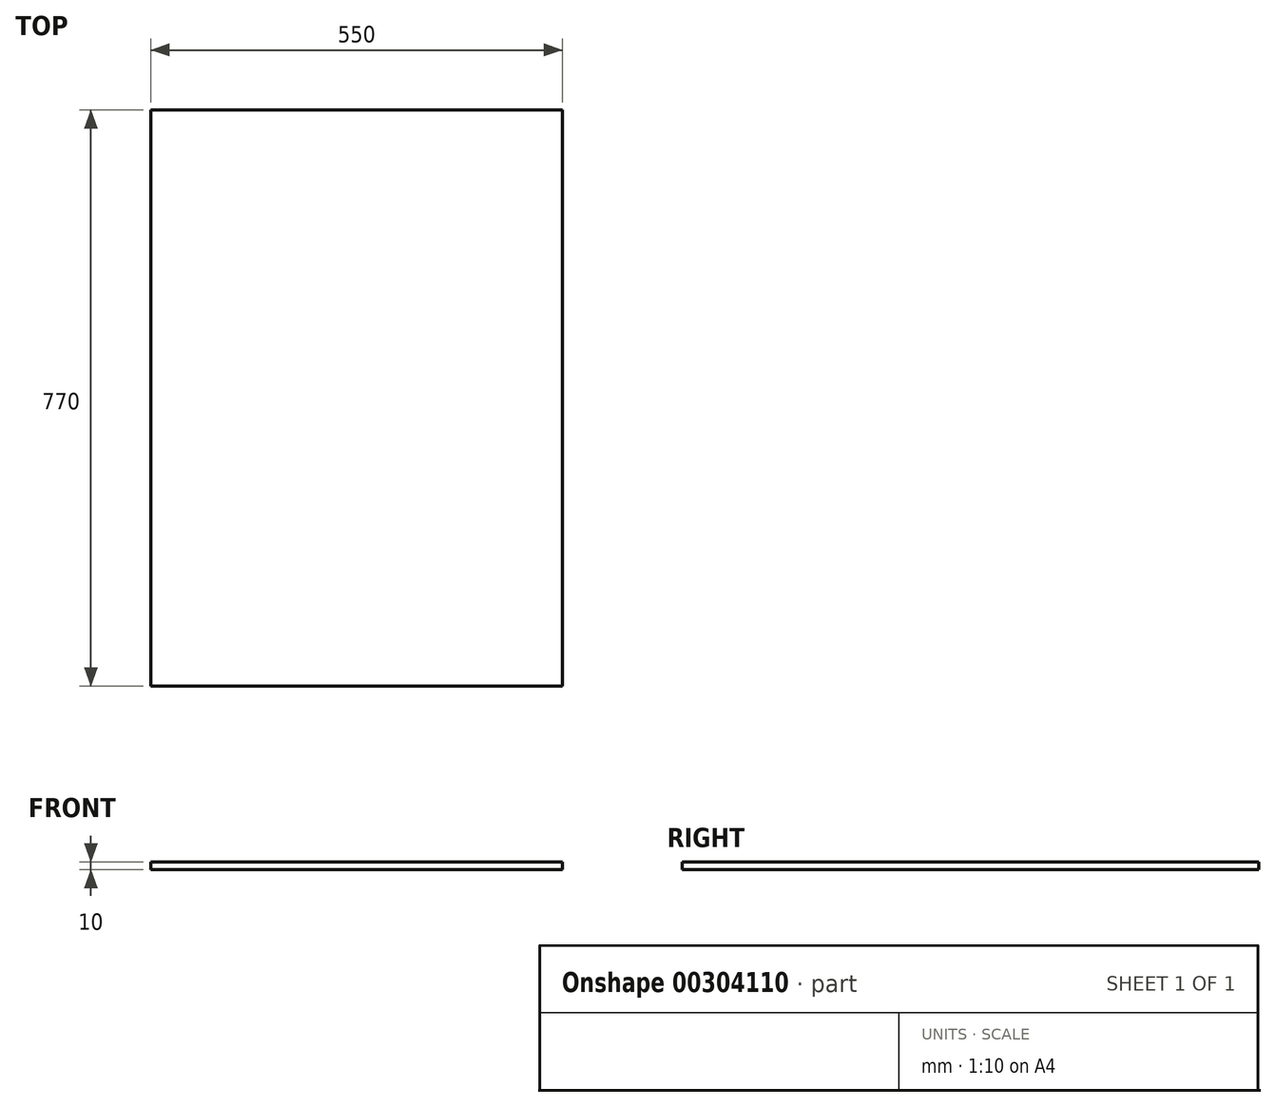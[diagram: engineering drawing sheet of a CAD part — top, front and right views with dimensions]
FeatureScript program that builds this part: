
annotation { "Feature Type Name" : "Feature", "Feature Type Description" : "" }
export const myFeature = defineFeature(function(context is Context, id is Id, definition is map)
    precondition{}
    {
        {
            var Q0;
            Q0=qCreatedBy(makeId("Top.planeOp"),FACE);
            var sketch = newSketch(context, id + "F0", { "sketchPlane" : qUnion([Q0])});
            skLineSegment(sketch, "E0.bottom", {"start": v(-274.6, 546.4) * mm, "end": v(275.4, 546.4) * mm});
            skLineSegment(sketch, "E0.top", {"start": v(-274.6, -223.6) * mm, "end": v(275.4, -223.6) * mm});
            skLineSegment(sketch, "E0.left", {"start": v(-274.6, 546.4) * mm, "end": v(-274.6, -223.6) * mm});
            skLineSegment(sketch, "E0.right", {"start": v(275.4, 546.4) * mm, "end": v(275.4, -223.6) * mm});
            skSolve(sketch);
        }
        {
            var Q0;
            Q0=makeQuery(id+"F0.imprint","IMPRINT",FACE,{"disambiguationData":[TD([[makeQuery(id+"F0.imprint","IMPRINT",EDGE,{"derivedFrom":sQuery(id+"F0.wireOp",EDGE,"E0.bottom")}),-1.0]])]});
            extrude(context, id + "F1", {"entities" : qUnion([Q0]), "depth" : 10 * mm, "offsetDistance" : 25 * mm});
        }
    });
